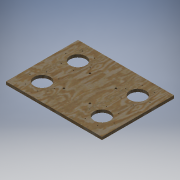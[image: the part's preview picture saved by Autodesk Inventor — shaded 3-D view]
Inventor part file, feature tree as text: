
AUTODESK INVENTOR PART (.ipt)
format: ipt  version: 2017 (Build 210142000, 142)  size: 184,320 bytes
history: native  units: in
note: dims shown in document units (in); Inventor stores cm internally (conversion verified against a paired STEP export)
features: sketch x4, hole x3, mirror x2, extrude x1
ambient origin geometry x8: Origin, YZ Plane, XZ Plane, XY Plane, X Axis, Y Axis, Z Axis, Center Point
bodies: Solid1 (feature_tree)
feature tree (10):
  sketch  "Sketch1"  dims[d0=24.0in d1=18.0in]
  sketch  "Sketch2"  dims[d4=24.0in d5=18.0in d6=24.0in d7=18.0in d8=24.0in d9=18.0in]
  extrude  "Extrusion1"  Depth=18.0in
  hole  "Hole1"  [1 undecoded]
  hole  "Hole2"  [1 undecoded]
  mirror  "Mirror1"
  mirror  "Mirror2"
  hole  "Hole4"  [1 undecoded]
  sketch  "Sketch3"  dims[d10=0.7in d11=0.0in]
  sketch  "Sketch5"  dims[d12=0.25in d13=0.75in d14=0.375in d15=0.25in d16=0.5635in d17=0.7in d18=0.0in d19=4.0in d20=0.75in d21=0.375in d22=0.25in d23=0.5635in d24=1.8125in d25=0.0in d41=4.602in d42=45.0deg d43=4.602in d44=4.602in d45=135.0deg d46=4.602in d47=45.0deg d48=0.5in d49=0.5in d50=0.5in d51=0.5in d52=0.5in d53=0.75in d54=0.375in d55=0.25in d56=0.5635in d57=1.0in d58=0.8108in]
note: 3 required parameter values undecoded (feature->parameter linkage not recoverable at this tier; creation-order binding heuristic only, values carry confidence <= 0.55)
